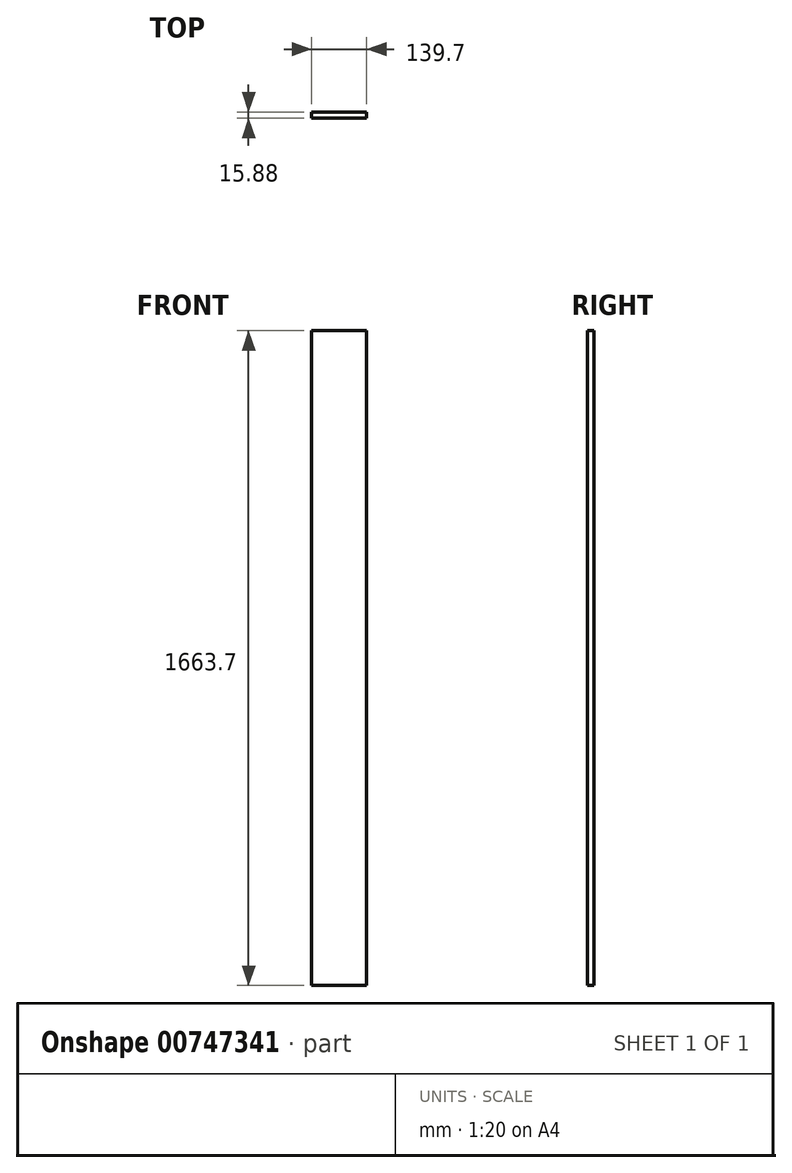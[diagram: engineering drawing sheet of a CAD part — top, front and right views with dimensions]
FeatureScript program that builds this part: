
annotation { "Feature Type Name" : "Feature", "Feature Type Description" : "" }
export const myFeature = defineFeature(function(context is Context, id is Id, definition is map)
    precondition{}
    {
        {
            var Q0;
            Q0=qCreatedBy(makeId("Front.planeOp"),FACE);
            var sketch = newSketch(context, id + "F0", { "sketchPlane" : qUnion([Q0])});
            skLineSegment(sketch, "E0.bottom", {"start": v(0, 0) * mm, "end": v(139.7, 0) * mm});
            skLineSegment(sketch, "E0.top", {"start": v(0, 1663.7) * mm, "end": v(139.7, 1663.7) * mm});
            skLineSegment(sketch, "E0.left", {"start": v(0, 0) * mm, "end": v(0, 1663.7) * mm});
            skLineSegment(sketch, "E0.right", {"start": v(139.7, 0) * mm, "end": v(139.7, 1663.7) * mm});
            skSolve(sketch);
        }
        {
            var Q0;
            Q0=makeQuery(id+"F0.imprint","IMPRINT",FACE,{"disambiguationData":[TD([[makeQuery(id+"F0.imprint","IMPRINT",EDGE,{"derivedFrom":sQuery(id+"F0.wireOp",EDGE,"E0.bottom")}),1.0]])]});
            extrude(context, id + "F1", {"entities" : qUnion([Q0]), "depth" : 15.88 * mm, "offsetDistance" : 25.4 * mm});
        }
    });
